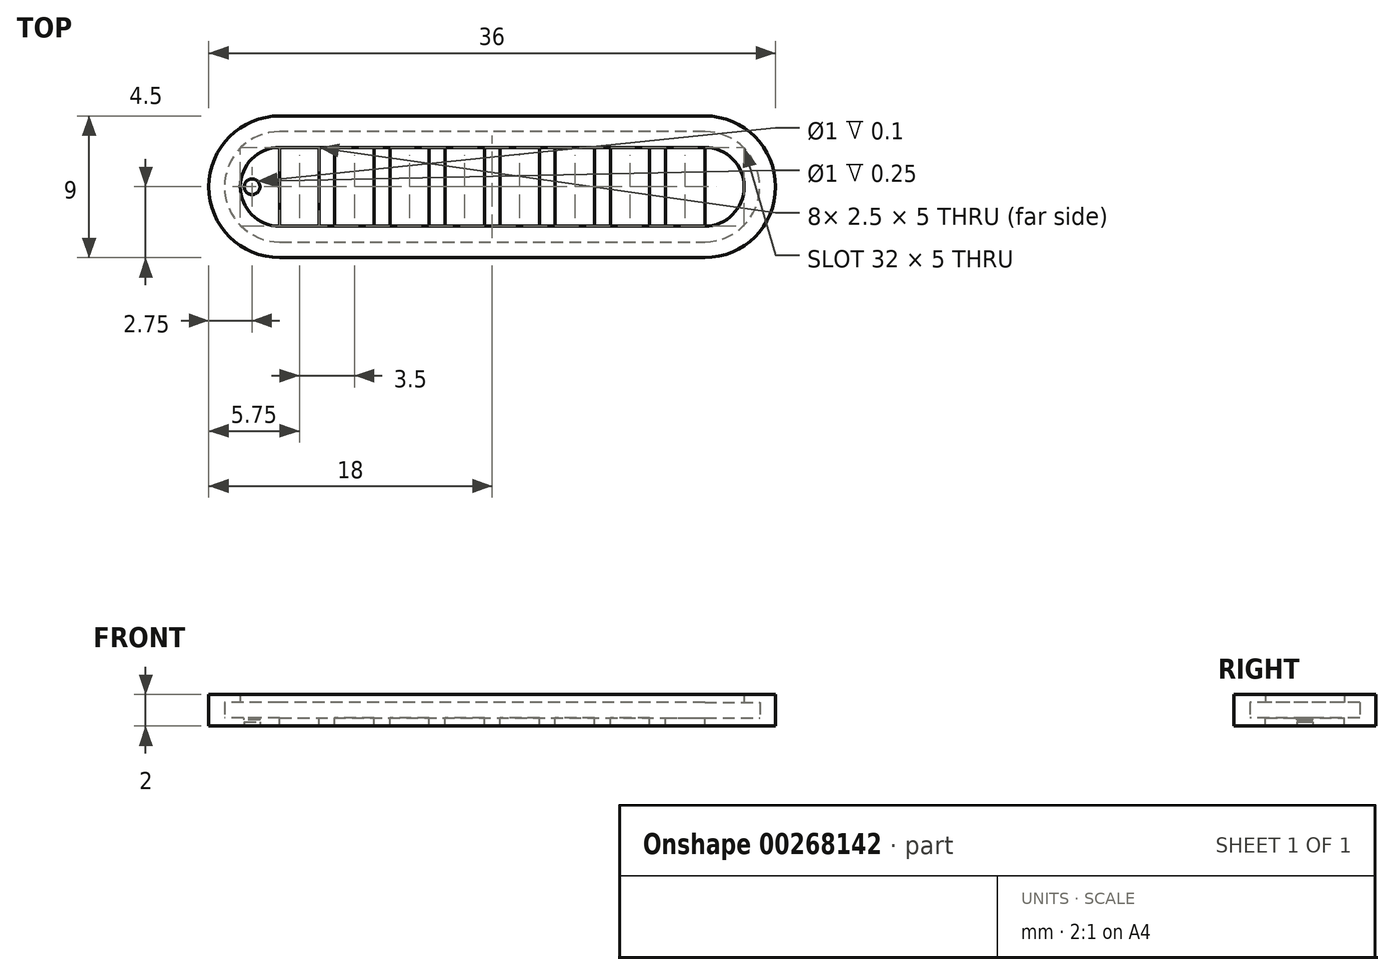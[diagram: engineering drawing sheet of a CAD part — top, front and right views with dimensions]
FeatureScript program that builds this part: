
annotation { "Feature Type Name" : "Feature", "Feature Type Description" : "" }
export const myFeature = defineFeature(function(context is Context, id is Id, definition is map)
    precondition{}
    {
        {
            var Q0;
            Q0=qCreatedBy(makeId("Top.planeOp"),FACE);
            var sketch = newSketch(context, id + "F0", { "sketchPlane" : qUnion([Q0])});
            skArc(sketch, "E0", {"start": v(-13.5, 4.5) * mm, "mid": v(-18, 0) * mm, "end": v(-13.5, -4.5) * mm});
            skArc(sketch, "E1", {"start": v(13.5, -4.5) * mm, "mid": v(18, 0) * mm, "end": v(13.5, 4.5) * mm});
            skLineSegment(sketch, "E2", {"start": v(0, 4.5) * mm, "end": v(-13.5, 4.5) * mm});
            skLineSegment(sketch, "E3", {"start": v(0, 4.5) * mm, "end": v(13.5, 4.5) * mm});
            skLineSegment(sketch, "E4", {"start": v(0, -4.5) * mm, "end": v(-13.5, -4.5) * mm});
            skLineSegment(sketch, "E5", {"start": v(0, -4.5) * mm, "end": v(13.5, -4.5) * mm});
            skSolve(sketch);
        }
        {
            var Q0;
            Q0=makeQuery(id+"F0.imprint","IMPRINT",FACE,{"disambiguationData":[TD([[makeQuery(id+"F0.imprint","IMPRINT",EDGE,{"derivedFrom":sQuery(id+"F0.wireOp",EDGE,"E0")}),1.0]])]});
            extrude(context, id + "F1", {"entities" : qUnion([Q0]), "depth" : 0.5 * mm, "offsetDistance" : 25 * mm});
        }
        {
            var Q0;
            Q0=makeQuery(id+"F1.opExtrude","CAP_FACE",FACE,{"disambiguationData":[OSD([sQuery(id+"F0.wireOp",EDGE,"E0"),sQuery(id+"F0.wireOp",EDGE,"E1"),sQuery(id+"F0.wireOp",EDGE,"E2"),sQuery(id+"F0.wireOp",EDGE,"E3"),sQuery(id+"F0.wireOp",EDGE,"E4"),sQuery(id+"F0.wireOp",EDGE,"E5")])],"isStart":false});
            var sketch = newSketch(context, id + "F2", { "sketchPlane" : qUnion([Q0])});
            skLineSegment(sketch, "E6.left", {"start": v(-13.5, 2.5) * mm, "end": v(-13.5, -2.5) * mm});
            skLineSegment(sketch, "E7", {"start": v(-13.5, 2.5) * mm, "end": v(-11, 2.5) * mm});
            skLineSegment(sketch, "E8", {"start": v(-11, 2.5) * mm, "end": v(-11, -2.5) * mm});
            skLineSegment(sketch, "E9", {"start": v(-11, -2.5) * mm, "end": v(-13.5, -2.5) * mm});
            skArc(sketch, "E10", {"start": v(-13.5, 4.5) * mm, "mid": v(-18, 0) * mm, "end": v(-13.5, -4.5) * mm});
            skArc(sketch, "E11", {"start": v(13.5, -4.5) * mm, "mid": v(18, 0) * mm, "end": v(13.5, 4.5) * mm});
            skLineSegment(sketch, "E12", {"start": v(0, 4.5) * mm, "end": v(-13.5, 4.5) * mm});
            skLineSegment(sketch, "E13", {"start": v(0, 4.5) * mm, "end": v(13.5, 4.5) * mm});
            skLineSegment(sketch, "E14", {"start": v(0, -4.5) * mm, "end": v(-13.5, -4.5) * mm});
            skLineSegment(sketch, "E15", {"start": v(0, -4.5) * mm, "end": v(13.5, -4.5) * mm});
            skArc(sketch, "E16", {"start": v(-13.5, 3.5) * mm, "mid": v(-17, 0) * mm, "end": v(-13.5, -3.5) * mm});
            skLineSegment(sketch, "E17", {"start": v(0, 3.5) * mm, "end": v(13.5, 3.5) * mm});
            skLineSegment(sketch, "E18", {"start": v(0, -3.5) * mm, "end": v(13.5, -3.5) * mm});
            skLineSegment(sketch, "E19", {"start": v(0, -3.5) * mm, "end": v(-13.5, -3.5) * mm});
            skLineSegment(sketch, "E20", {"start": v(0, 3.5) * mm, "end": v(-13.5, 3.5) * mm});
            skArc(sketch, "E21.trimOffspring", {"start": v(13.5, -3.5) * mm, "mid": v(17, 0) * mm, "end": v(13.5, 3.5) * mm});
            skLineSegment(sketch, "E22", {"start": v(-10, 2.5) * mm, "end": v(-7.5, 2.5) * mm});
            skLineSegment(sketch, "E23", {"start": v(-6.5, 2.5) * mm, "end": v(-4, 2.5) * mm});
            skLineSegment(sketch, "E24", {"start": v(-3, 2.5) * mm, "end": v(-0.5, 2.5) * mm});
            skLineSegment(sketch, "E25", {"start": v(0.5, 2.5) * mm, "end": v(3, 2.5) * mm});
            skLineSegment(sketch, "E26", {"start": v(4, 2.5) * mm, "end": v(6.5, 2.5) * mm});
            skLineSegment(sketch, "E27", {"start": v(7.5, 2.5) * mm, "end": v(10, 2.5) * mm});
            skLineSegment(sketch, "E28", {"start": v(11, 2.5) * mm, "end": v(13.5, 2.5) * mm});
            skLineSegment(sketch, "E29", {"start": v(13.5, 2.5) * mm, "end": v(13.5, -2.5) * mm});
            skLineSegment(sketch, "E30", {"start": v(13.5, -2.5) * mm, "end": v(11, -2.5) * mm});
            skLineSegment(sketch, "E31", {"start": v(10, -2.5) * mm, "end": v(7.5, -2.5) * mm});
            skLineSegment(sketch, "E32", {"start": v(6.5, -2.5) * mm, "end": v(4, -2.5) * mm});
            skLineSegment(sketch, "E33", {"start": v(3, -2.5) * mm, "end": v(0.5, -2.5) * mm});
            skLineSegment(sketch, "E34", {"start": v(-0.5, -2.5) * mm, "end": v(-3, -2.5) * mm});
            skLineSegment(sketch, "E35", {"start": v(-4, -2.5) * mm, "end": v(-6.5, -2.5) * mm});
            skLineSegment(sketch, "E36", {"start": v(-7.5, -2.5) * mm, "end": v(-10, -2.5) * mm});
            skLineSegment(sketch, "E37", {"start": v(-10, -2.5) * mm, "end": v(-10, 2.5) * mm});
            skLineSegment(sketch, "E38", {"start": v(-7.5, 2.5) * mm, "end": v(-7.5, -2.5) * mm});
            skLineSegment(sketch, "E39", {"start": v(-6.5, -2.5) * mm, "end": v(-6.5, 2.5) * mm});
            skLineSegment(sketch, "E40", {"start": v(-4, 2.5) * mm, "end": v(-4, -2.5) * mm});
            skLineSegment(sketch, "E41", {"start": v(-3, -2.5) * mm, "end": v(-3, 2.5) * mm});
            skLineSegment(sketch, "E42", {"start": v(-0.5, 2.5) * mm, "end": v(-0.5, -2.5) * mm});
            skLineSegment(sketch, "E43", {"start": v(0.5, -2.5) * mm, "end": v(0.5, 2.5) * mm});
            skLineSegment(sketch, "E44", {"start": v(3, 2.5) * mm, "end": v(3, -2.5) * mm});
            skLineSegment(sketch, "E45", {"start": v(4, -2.5) * mm, "end": v(4, 2.5) * mm});
            skLineSegment(sketch, "E46", {"start": v(6.5, 2.5) * mm, "end": v(6.5, -2.5) * mm});
            skLineSegment(sketch, "E47", {"start": v(7.5, -2.5) * mm, "end": v(7.5, 2.5) * mm});
            skLineSegment(sketch, "E48", {"start": v(10, 2.5) * mm, "end": v(10, -2.5) * mm});
            skLineSegment(sketch, "E49", {"start": v(11, -2.5) * mm, "end": v(11, 2.5) * mm});
            skSolve(sketch);
        }
        {
            var Q0;
            Q0=makeQuery(id+"F2.imprint","IMPRINT",FACE,{"disambiguationData":[TD([[makeQuery(id+"F2.imprint","IMPRINT",EDGE,{"derivedFrom":sQuery(id+"F2.wireOp",EDGE,"E6.left")}),1.0]])]});
            var Q1;
            Q1=makeQuery(id+"F2.imprint","IMPRINT",FACE,{"disambiguationData":[TD([[makeQuery(id+"F2.imprint","IMPRINT",EDGE,{"derivedFrom":sQuery(id+"F2.wireOp",EDGE,"4549057b-0e14-440c-a34f-5f6b0ecd6914")}),-1.0]])]});
            var Q2;
            Q2=makeQuery(id+"F2.imprint","IMPRINT",FACE,{"disambiguationData":[TD([[makeQuery(id+"F2.imprint","IMPRINT",EDGE,{"derivedFrom":sQuery(id+"F2.wireOp",EDGE,"178067d5-5b30-4ee7-83d7-d6204dece448")}),-1.0]])]});
            var Q3;
            Q3=makeQuery(id+"F2.imprint","IMPRINT",FACE,{"disambiguationData":[TD([[makeQuery(id+"F2.imprint","IMPRINT",EDGE,{"derivedFrom":sQuery(id+"F2.wireOp",EDGE,"3b1b2400-ed5c-4165-9aaa-1df116534781")}),-1.0]])]});
            var Q4;
            Q4=makeQuery(id+"F2.imprint","IMPRINT",FACE,{"disambiguationData":[TD([[makeQuery(id+"F2.imprint","IMPRINT",EDGE,{"derivedFrom":sQuery(id+"F2.wireOp",EDGE,"9a1f8aea-bcc2-459a-a10a-435305c535ae")}),-1.0]])]});
            var Q5;
            Q5=makeQuery(id+"F2.imprint","IMPRINT",FACE,{"disambiguationData":[TD([[makeQuery(id+"F2.imprint","IMPRINT",EDGE,{"derivedFrom":sQuery(id+"F2.wireOp",EDGE,"76538429-ef45-47d1-ab75-bf2f9038f2d2")}),-1.0]])]});
            var Q6;
            Q6=makeQuery(id+"F2.imprint","IMPRINT",FACE,{"disambiguationData":[TD([[makeQuery(id+"F2.imprint","IMPRINT",EDGE,{"derivedFrom":sQuery(id+"F2.wireOp",EDGE,"360b03a7-372c-4756-baae-9c028e933fb2")}),-1.0]])]});
            var Q7;
            Q7=makeQuery(id+"F2.imprint","IMPRINT",FACE,{"disambiguationData":[TD([[makeQuery(id+"F2.imprint","IMPRINT",EDGE,{"derivedFrom":sQuery(id+"F2.wireOp",EDGE,"E6.right")}),-1.0]])]});
            var Q8;
            Q8=makeQuery(id+"F2.imprint","IMPRINT",FACE,{"disambiguationData":[TD([[makeQuery(id+"F2.imprint","IMPRINT",EDGE,{"derivedFrom":sQuery(id+"F2.wireOp",EDGE,"E23")}),-1.0]])]});
            var Q9;
            Q9=makeQuery(id+"F2.imprint","IMPRINT",FACE,{"disambiguationData":[TD([[makeQuery(id+"F2.imprint","IMPRINT",EDGE,{"derivedFrom":sQuery(id+"F2.wireOp",EDGE,"E24")}),-1.0]])]});
            var Q10;
            Q10=makeQuery(id+"F2.imprint","IMPRINT",FACE,{"disambiguationData":[TD([[makeQuery(id+"F2.imprint","IMPRINT",EDGE,{"derivedFrom":sQuery(id+"F2.wireOp",EDGE,"E22")}),-1.0]])]});
            var Q11;
            Q11=makeQuery(id+"F2.imprint","IMPRINT",FACE,{"disambiguationData":[TD([[makeQuery(id+"F2.imprint","IMPRINT",EDGE,{"derivedFrom":sQuery(id+"F2.wireOp",EDGE,"E25")}),-1.0]])]});
            var Q12;
            Q12=makeQuery(id+"F2.imprint","IMPRINT",FACE,{"disambiguationData":[TD([[makeQuery(id+"F2.imprint","IMPRINT",EDGE,{"derivedFrom":sQuery(id+"F2.wireOp",EDGE,"E26")}),-1.0]])]});
            var Q13;
            Q13=makeQuery(id+"F2.imprint","IMPRINT",FACE,{"disambiguationData":[TD([[makeQuery(id+"F2.imprint","IMPRINT",EDGE,{"derivedFrom":sQuery(id+"F2.wireOp",EDGE,"E27")}),-1.0]])]});
            var Q14;
            Q14=makeQuery(id+"F2.imprint","IMPRINT",FACE,{"disambiguationData":[TD([[makeQuery(id+"F2.imprint","IMPRINT",EDGE,{"derivedFrom":sQuery(id+"F2.wireOp",EDGE,"E28")}),-1.0]])]});
            extrude(context, id + "F3", {"entities" : qUnion([Q0, Q1, Q2, Q3, Q4, Q5, Q6, Q7, Q8, Q9, Q10, Q11, Q12, Q13, Q14]), "operationType" : NewBodyOperationType.REMOVE, "endBound" : BoundingType.THROUGH_ALL, "oppositeDirection" : true, "depth" : 1.2 * mm, "offsetDistance" : 25 * mm});
        }
        {
            var Q0;
            Q0=makeQuery(id+"F2.imprint","IMPRINT",FACE,{"disambiguationData":[TD([[makeQuery(id+"F2.imprint","IMPRINT",EDGE,{"derivedFrom":sQuery(id+"F2.wireOp",EDGE,"E10")}),1.0]])]});
            extrude(context, id + "F4", {"entities" : qUnion([Q0]), "operationType" : NewBodyOperationType.ADD, "depth" : 1 * mm, "offsetDistance" : 25 * mm});
        }
        {
            var Q0;
            Q0=makeQuery(id+"F4.opExtrude","CAP_FACE",FACE,{"disambiguationData":[OSD([sQuery(id+"F2.wireOp",EDGE,"E10"),sQuery(id+"F2.wireOp",EDGE,"E11"),sQuery(id+"F2.wireOp",EDGE,"E12"),sQuery(id+"F2.wireOp",EDGE,"E13"),sQuery(id+"F2.wireOp",EDGE,"E14"),sQuery(id+"F2.wireOp",EDGE,"E15"),sQuery(id+"F2.wireOp",EDGE,"E16"),sQuery(id+"F2.wireOp",EDGE,"E17"),sQuery(id+"F2.wireOp",EDGE,"E18"),sQuery(id+"F2.wireOp",EDGE,"E19"),sQuery(id+"F2.wireOp",EDGE,"E20"),sQuery(id+"F2.wireOp",EDGE,"E21.trimOffspring")])],"isStart":false});
            var sketch = newSketch(context, id + "F5", { "sketchPlane" : qUnion([Q0])});
            skArc(sketch, "E50", {"start": v(-13.5, 4.5) * mm, "mid": v(-18, 0) * mm, "end": v(-13.5, -4.5) * mm});
            skArc(sketch, "E51", {"start": v(13.5, -4.5) * mm, "mid": v(18, 0) * mm, "end": v(13.5, 4.5) * mm});
            skLineSegment(sketch, "E52", {"start": v(0, 4.5) * mm, "end": v(-13.5, 4.5) * mm});
            skLineSegment(sketch, "E53", {"start": v(0, 4.5) * mm, "end": v(13.5, 4.5) * mm});
            skLineSegment(sketch, "E54", {"start": v(0, -4.5) * mm, "end": v(-13.5, -4.5) * mm});
            skLineSegment(sketch, "E55", {"start": v(0, -4.5) * mm, "end": v(13.5, -4.5) * mm});
            skArc(sketch, "E56", {"start": v(-13.5, 2.5) * mm, "mid": v(-16, 0) * mm, "end": v(-13.5, -2.5) * mm});
            skArc(sketch, "E57", {"start": v(13.5, -2.5) * mm, "mid": v(16, 0) * mm, "end": v(13.5, 2.5) * mm});
            skLineSegment(sketch, "E58", {"start": v(0, 2.5) * mm, "end": v(-13.5, 2.5) * mm});
            skLineSegment(sketch, "E59", {"start": v(0, -2.5) * mm, "end": v(-13.5, -2.5) * mm});
            skLineSegment(sketch, "E60", {"start": v(0, -2.5) * mm, "end": v(13.5, -2.5) * mm});
            skLineSegment(sketch, "E61", {"start": v(0, 2.5) * mm, "end": v(13.5, 2.5) * mm});
            skSolve(sketch);
        }
        {
            var Q0;
            Q0=makeQuery(id+"F5.imprint","IMPRINT",FACE,{"disambiguationData":[TD([[makeQuery(id+"F5.imprint","IMPRINT",EDGE,{"derivedFrom":sQuery(id+"F5.wireOp",EDGE,"E50")}),1.0]])]});
            var Q1;
            Q1=makeQuery(id+"F5.imprint","IMPRINT",FACE,{"disambiguationData":[TD([[makeQuery(id+"F5.imprint","IMPRINT",EDGE,{"derivedFrom":sQuery(id+"F5.wireOp",EDGE,"E56")}),-1.0]])]});
            extrude(context, id + "F6", {"entities" : qUnion([Q0, Q1]), "operationType" : NewBodyOperationType.ADD, "depth" : 0.5 * mm, "offsetDistance" : 25 * mm});
        }
        {
            var Q0;
            Q0=makeQuery(id+"F1.opExtrude","CAP_FACE",FACE,{"disambiguationData":[OSD([sQuery(id+"F0.wireOp",EDGE,"E0"),sQuery(id+"F0.wireOp",EDGE,"E1"),sQuery(id+"F0.wireOp",EDGE,"E2"),sQuery(id+"F0.wireOp",EDGE,"E3"),sQuery(id+"F0.wireOp",EDGE,"E4"),sQuery(id+"F0.wireOp",EDGE,"E5")])],"isStart":false});
            var sketch = newSketch(context, id + "F7", { "sketchPlane" : qUnion([Q0])});
            skLineSegment(sketch, "E62", {"start": v(-17, 0) * mm, "end": v(-15.25, 0) * mm});
            skCircle(sketch, "E63", {"center": v(-15.25, 0) * mm, "radius": 0.5 * mm});
            skSolve(sketch);
        }
        {
            var Q0;
            Q0 = qSketchRegion(id + "F7", true);
            extrude(context, id + "F8", {"entities" : qUnion([Q0]), "operationType" : NewBodyOperationType.REMOVE, "oppositeDirection" : true, "depth" : 0.1 * mm, "offsetDistance" : 25 * mm});
        }
        {
            var Q0;
            Q0=makeQuery(id+"F1.opExtrude","CAP_FACE",FACE,{"disambiguationData":[OSD([sQuery(id+"F0.wireOp",EDGE,"E0"),sQuery(id+"F0.wireOp",EDGE,"E1"),sQuery(id+"F0.wireOp",EDGE,"E2"),sQuery(id+"F0.wireOp",EDGE,"E3"),sQuery(id+"F0.wireOp",EDGE,"E4"),sQuery(id+"F0.wireOp",EDGE,"E5")])],"isStart":true});
            var sketch = newSketch(context, id + "F9", { "sketchPlane" : qUnion([Q0])});
            skLineSegment(sketch, "E64", {"start": v(-18, 0) * mm, "end": v(-15.25, 0) * mm});
            skCircle(sketch, "E65", {"center": v(-15.25, 0) * mm, "radius": 0.5 * mm});
            skSolve(sketch);
        }
        {
            var Q0;
            Q0 = qSketchRegion(id + "F9", true);
            extrude(context, id + "F10", {"entities" : qUnion([Q0]), "operationType" : NewBodyOperationType.REMOVE, "oppositeDirection" : true, "depth" : 0.25 * mm, "offsetDistance" : 25 * mm});
        }
    });
